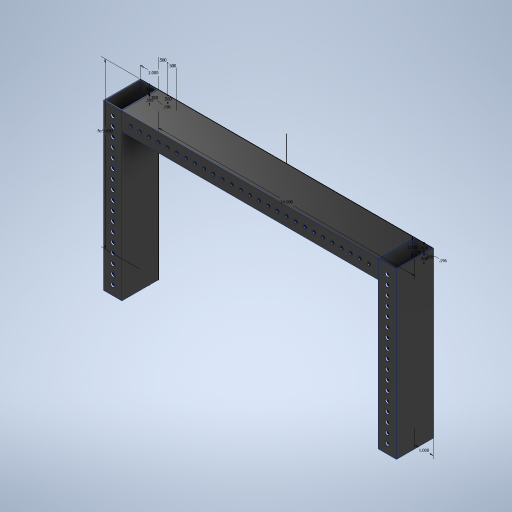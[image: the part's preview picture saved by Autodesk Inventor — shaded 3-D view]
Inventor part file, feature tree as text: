
AUTODESK INVENTOR PART (.ipt)
format: ipt  version: 2024 (Build 280153000, 153)  size: 517,120 bytes
history: native  units: in
note: dims shown in document units (in); Inventor stores cm internally (conversion verified against a paired STEP export)
features: extrude x9, sketch x5, projected_geometry x4, other x3
ambient origin geometry x8: Origin, YZ Plane, XZ Plane, XY Plane, X Axis, Y Axis, Z Axis, Center Point
bodies: Body1 (feature_tree), Body2 (feature_tree), Body3 (feature_tree)
feature tree (21):
  other  "2024-220-001-Right-Stop-Support"
  sketch  "Sketch1"  dims[d0=1.0in d2=14.0in]
  extrude  "Extrusion1"  Depth=14.0in
  extrude  "Extrusion2"  Depth=1.0in
  extrude  "Extrusion3"  Depth=2.0in TaperAngle=0.0deg
  extrude  "Extrusion4"  Depth=0.0625in
  extrude  "Extrusion5"  Depth=0.0625in
  extrude  "Extrusion6"  Depth=1.0in TaperAngle=0.0deg
  extrude  "Extrusion7"  Depth=0.0625in
  extrude  "Extrusion8"  Depth=1.0in TaperAngle=0.0deg
  extrude  "Extrusion9"  Depth=0.0625in
  other  "2024-220-002-Shootaur-Rest"
  other  "2024-220-003-Left-Stop-Support"
  sketch  "Sketch2"  dims[d3=1.0in d4=1.0in]
  projected_geometry  "Projected Loop1"
  sketch  "Sketch3"  dims[d32=2.0in d33=0.0in d34=2.0in d35=0.0in]
  projected_geometry  "Projected Loop2"
  sketch  "Sketch4"  dims[d36=2.0in d37=0.0in d38=0.0625in]
  projected_geometry  "Projected Loop3"
  sketch  "Sketch5"  dims[d39=12.6875in d40=0.0in d41=0.0625in d42=12.6875in d43=0.0in d44=0.0625in d45=11.0in d46=0.0in d54=0.0625in d55=4.6875in d56=0.0in d64=0.5in d65=0.5in d66=10.6299in d68=0.5in d69=0.3937in d71=1.0in d73=9.0in d75=0.196in d76=0.5in d77=0.5in d78=6.6929in d80=0.5in d81=0.3937in d83=1.0in d85=0.196in d86=0.5in d87=0.5in d88=6.6929in d90=0.5in d91=0.3937in d93=1.0in d95=2.5in d96=0.0in d97=2.5in d98=0.0in]
  projected_geometry  "Projected Loop4"
